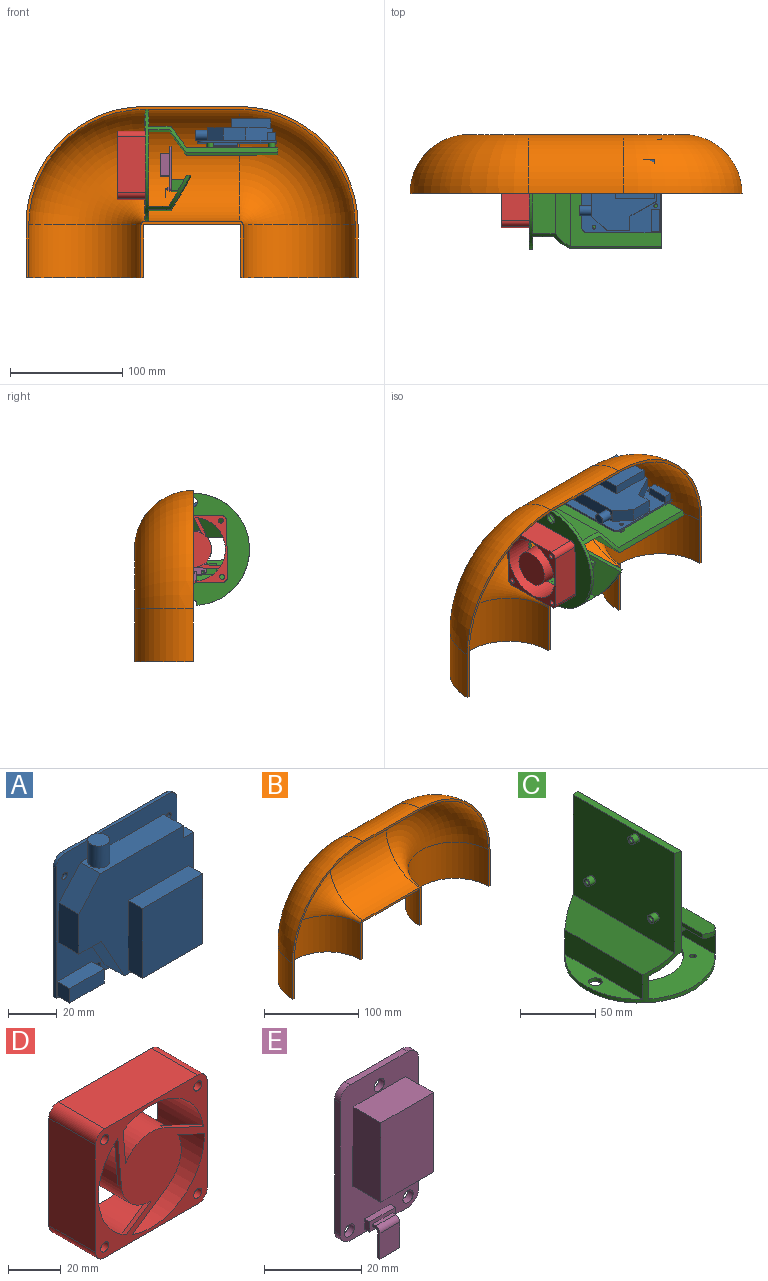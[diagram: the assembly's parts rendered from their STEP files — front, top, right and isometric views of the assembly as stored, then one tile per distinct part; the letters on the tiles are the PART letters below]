
ASSEMBLY  parts=5 mates=4
PART A: 39 faces, bbox 70x24.3x72.1 mm
  f0: plane 65x1.6mm, normal (0,0,-1), area 104mm2, adj f2,f7,f9,f10
  f1: cylinder r=1.6mm len=3.2mm, axis (0,1,0), area 16.1mm2, adj f7,f9
  f2: plane 65x1.6mm, normal (-1,0,0), area 104mm2, adj f0,f7,f9,f37
  f3: plane 60x1.6mm, normal (1,0,0), area 96mm2, adj f4,f7,f9,f10
  f4: cylinder r=5mm len=5mm, axis (0,1,0), area 12.6mm2, adj f3,f7,f9,f38
  f5: cylinder r=1.6mm len=3.2mm, axis (0,1,0), area 16.1mm2, adj f7,f9
  f6: cylinder r=1.6mm len=3.2mm, axis (0,1,0), area 16.1mm2, adj f7,f9
  f7: plane 70x70mm, normal (0,-1,0), area 1459.9mm2, adj f0,f1,f2,f3,f4,f5,f6,f10
  f8: plane 25x3mm, normal (0,0,1), area 75mm2, adj f9,f28,f29,f31
  f9: plane 70x70mm, normal (0,1,0), area 4234.8mm2, adj f0,f1,f2,f3,f4,f5,f6,f8
  f10: cylinder r=5mm len=5mm, axis (0,1,0), area 12.6mm2, adj f0,f3,f7,f9
  f11: plane 14.1x12.5mm, normal (-0.75,0,0.66), area 216.7mm2, adj f7,f12,f24,f27
  f12: plane 20x11.5mm, normal (-1,0,0), area 230mm2, adj f7,f11,f13,f24
  f13: plane 13x11.5mm, normal (0,0,-1), area 149.5mm2, adj f7,f12,f14,f24
  f14: plane 24x13.3mm, normal (-0.87,0,-0.48), area 315.5mm2, adj f7,f13,f15,f24
  f15: plane 40x11.5mm, normal (0,0,-1), area 460mm2, adj f7,f14,f16,f24
  f16: plane 52x11.5mm, normal (1,0,0), area 598mm2, adj f7,f15,f17,f24
  f17: plane 11.5x5.8mm, normal (0,0,1), area 66.7mm2, adj f7,f16,f18,f24
  f18: plane 11.5x6.1mm, normal (1,0,0), area 70.2mm2, adj f7,f17,f24,f27
  f19: plane 35x8.2mm, normal (1,0,0), area 287mm2, adj f20,f22,f23,f24
  f20: plane 35x8.2mm, normal (0,0,1), area 287mm2, adj f19,f21,f23,f24
  f21: plane 35x8.2mm, normal (-1,0,0), area 287mm2, adj f20,f22,f23,f24
  f22: plane 35x8.2mm, normal (0,0,-1), area 287mm2, adj f19,f21,f23,f24
  f23: plane 35x35mm, normal (0,-1,0), area 1225mm2, adj f19,f20,f21,f22
  f24: plane 66.3x58.1mm, normal (0,-1,0), area 2031.9mm2, adj f11,f12,f13,f14,f15,f16,f17,f18
  f25: cylinder r=4.5mm len=11mm, axis (0,0,1), area 311mm2, adj f26,f27
  f26: plane 9x9mm, normal (0,0,1), area 63.6mm2, adj f25
  f27: plane 48x11.5mm, normal (0,0,1), area 488.4mm2, adj f7,f11,f18,f24,f25
  f28: plane 25x25mm, normal (0,1,0), area 625mm2, adj f8,f29,f30,f31
  f29: plane 25x3mm, normal (-1,0,0), area 75mm2, adj f8,f9,f28,f30
  f30: plane 25x3mm, normal (0,0,-1), area 75mm2, adj f9,f28,f29,f31
  f31: plane 25x3mm, normal (1,0,0), area 75mm2, adj f8,f9,f28,f30
  f32: plane 20x7.2mm, normal (0,0,-1), area 144mm2, adj f7,f33,f35,f36
  f33: plane 7.2x7.15mm, normal (1,0,0), area 51.5mm2, adj f7,f32,f34,f36
  f34: plane 20x7.2mm, normal (0,0,1), area 144mm2, adj f7,f33,f35,f36
  f35: plane 7.2x7.15mm, normal (-1,0,0), area 51.5mm2, adj f7,f32,f34,f36
  f36: plane 20x7.15mm, normal (0,-1,0), area 143mm2, adj f32,f33,f34,f35
  f37: cylinder r=5mm len=5mm, axis (0,1,0), area 12.6mm2, adj f2,f7,f9,f38
  f38: plane 60x1.6mm, normal (0,0,1), area 96mm2, adj f4,f7,f9,f37
PART B: 14 faces, bbox 313.4x89.8x161.2 mm
  f0: plane 91x50mm, normal (0,-1,0), area 461.2mm2, adj f1,f2,f3,f4,f5,f6,f7,f8
  f1: cylinder r=52.5mm len=105mm, axis (0,0,-1), area 7751.9mm2, adj f0,f2,f6,f13
  f2: torus R=53mm, axis (0,1,0), area 13731.1mm2, adj f0,f1,f3,f13
  f3: cylinder r=52.5mm len=105mm, axis (1,0,0), area 14019.4mm2, adj f0,f2,f4,f13
  f4: torus R=53mm, axis (0,1,0), area 13731.1mm2, adj f0,f3,f5,f13
  f5: cylinder r=52.5mm len=105mm, axis (0,0,1), area 7751.9mm2, adj f0,f4,f7,f13
  f6: plane 105x52.5mm, normal (0,0,-1), area 402.5mm2, adj f0,f1,f8,f13
  f7: plane 105x52.5mm, normal (0,0,-1), area 402.5mm2, adj f0,f5,f12,f13
  f8: cylinder r=50mm len=100mm, axis (0,0,-1), area 7382.7mm2, adj f0,f6,f9,f13
  f9: torus R=53mm, axis (0,1,0), area 13077.2mm2, adj f0,f8,f10,f13
  f10: cylinder r=50mm len=100mm, axis (1,0,0), area 13351.8mm2, adj f0,f9,f11,f13
  f11: torus R=53mm, axis (0,1,0), area 13077.2mm2, adj f0,f10,f12,f13
  f12: cylinder r=50mm len=100mm, axis (0,0,1), area 7382.7mm2, adj f0,f7,f11,f13
  f13: plane 296x152.5mm, normal (0,-1,0), area 1266.3mm2, adj f1,f2,f3,f4,f5,f6,f7,f8
PART C: 47 faces, bbox 100x100x118 mm
  f0: plane 100x68mm, normal (0,0,1), area 3514.8mm2, adj f2,f5,f7,f8,f9,f11,f16,f22
  f1: plane 60x9.96mm, normal (0,0,1), area 394.5mm2, adj f2,f3,f4,f10,f17
  f2: cylinder r=50mm len=118mm, axis (0,0,1), area 2506.6mm2, adj f0,f1,f3,f10,f12,f13,f14,f15
  f3: plane 3x1.96mm, normal (0,1,0), area 5.9mm2, adj f1,f2,f4,f12
  f4: cylinder r=2mm len=4mm, axis (0,0,1), area 18.8mm2, adj f1,f3,f10,f12
  f5: cylinder r=2.15mm len=4.3mm, axis (0,0,1), area 40.5mm2, adj f0,f12
  f6: cylinder r=4.5mm len=9mm, axis (0,0,1), area 84.8mm2, adj f12,f13
  f7: cylinder r=2.15mm len=4.3mm, axis (0,0,1), area 40.5mm2, adj f0,f12
  f8: cylinder r=2.15mm len=4.3mm, axis (0,0,1), area 40.5mm2, adj f0,f12
  f9: cylinder r=29mm len=58mm, axis (0,0,1), area 546.6mm2, adj f0,f12
  f10: plane 3x1.96mm, normal (0,-1,0), area 5.9mm2, adj f1,f2,f4,f12
  f11: cylinder r=2.15mm len=4.3mm, axis (0,0,1), area 40.5mm2, adj f0,f12
  f12: plane 100x99.96mm, normal (0,0,-1), area 5076mm2, adj f2,f3,f4,f5,f6,f7,f8,f9
  f13: plane 73.32x16mm, normal (0,0,1), area 747.5mm2, adj f2,f6,f24
  f14: plane 97.98x30mm, normal (0.5,0,0.87), area 2915.6mm2, adj f2,f17,f18
  f15: plane 97.98x27mm, normal (-0.5,0,-0.87), area 2232.9mm2, adj f2,f16,f18,f26,f27,f29,f30
  f16: plane 67.26x18.27mm, normal (-1,0,0), area 1228.7mm2, adj f0,f2,f15
  f17: plane 60x20mm, normal (1,0,0), area 1200mm2, adj f1,f2,f14
  f18: plane 97.98x3.46mm, normal (-1,0,0), area 339.4mm2, adj f2,f14,f15
  f19: plane 97.98x5mm, normal (0,0,1), area 483.9mm2, adj f2,f21,f25
  f20: plane 97.98x21mm, normal (0.59,0,-0.81), area 2336.6mm2, adj f2,f21,f22
  f21: plane 97.98x81.38mm, normal (1,0,0), area 7973.5mm2, adj f2,f19,f20
  f22: plane 78.46x18.47mm, normal (1,0,0), area 1448.8mm2, adj f0,f2,f20
  f23: plane 95.39x19mm, normal (-0.59,0,0.81), area 2020.9mm2, adj f2,f24,f25
  f24: plane 73.32x20mm, normal (-1,0,0), area 1466.4mm2, adj f2,f13,f23
  f25: plane 95.39x81.29mm, normal (-1,0,0), area 7669.6mm2, adj f2,f19,f23,f36,f40,f44
  f26: plane 40x6.35mm, normal (1,0,0), area 254mm2, adj f15,f28,f29,f30
  f27: plane 40x12.12mm, normal (-1,0,0), area 485mm2, adj f15,f28,f29,f30
  f28: plane 40x10mm, normal (0,0,-1), area 388.5mm2, adj f26,f27,f29,f30,f31,f33
  f29: plane 12.12x10mm, normal (0,1,0), area 92.4mm2, adj f15,f26,f27,f28
  f30: plane 12.12x10mm, normal (0,-1,0), area 92.4mm2, adj f15,f26,f27,f28
  f31: cylinder r=1.35mm len=7mm, axis (0,0,-1), area 59.4mm2, adj f28,f32
  f32: cone r=0mm half-angle=59deg, axis (0,0,-1), area 6.7mm2, adj f31
  f33: cylinder r=1.35mm len=7mm, axis (0,0,-1), area 59.4mm2, adj f28,f34
  f34: cone r=0mm half-angle=59deg, axis (0,0,-1), area 6.7mm2, adj f33
  f35: cylinder r=1.6mm len=5mm, axis (1,0,0), area 50.3mm2, adj f37,f38
  f36: cylinder r=3mm len=6mm, axis (1,0,0), area 94.2mm2, adj f25,f37
  f37: plane 6x6mm, normal (-1,0,0), area 20.2mm2, adj f35,f36
  f38: plane 3.2x3.2mm, normal (-1,0,0), area 8mm2, adj f35
  f39: cylinder r=1.6mm len=5mm, axis (1,0,0), area 50.3mm2, adj f41,f42
  f40: cylinder r=3mm len=6mm, axis (1,0,0), area 94.2mm2, adj f25,f41
  f41: plane 6x6mm, normal (-1,0,0), area 20.2mm2, adj f39,f40
  f42: plane 3.2x3.2mm, normal (-1,0,0), area 8mm2, adj f39
  f43: cylinder r=1.6mm len=5mm, axis (1,0,0), area 50.3mm2, adj f45,f46
  f44: cylinder r=3mm len=6mm, axis (1,0,0), area 94.2mm2, adj f25,f45
  f45: plane 6x6mm, normal (-1,0,0), area 20.2mm2, adj f43,f44
  f46: plane 3.2x3.2mm, normal (-1,0,0), area 8mm2, adj f43
PART D: 26 faces, bbox 60x25x60 mm
  f0: plane 21.59x13.54mm, normal (0,1,0), area 54.3mm2, adj f2,f18,f21,f22
  f1: plane 25.47x4.14mm, normal (0,1,0), area 54.3mm2, adj f2,f17,f18,f23
  f2: cylinder r=28.5mm len=57mm, axis (0,-1,0), area 4455.8mm2, adj f0,f1,f15,f16,f17,f19,f20,f21
  f3: plane 50x25mm, normal (0,0,1), area 1250mm2, adj f4,f13,f15,f16
  f4: cylinder r=5mm len=25mm, axis (0,-1,0), area 196.3mm2, adj f3,f5,f15,f16
  f5: plane 50x25mm, normal (-1,0,0), area 1250mm2, adj f4,f6,f15,f16
  f6: cylinder r=5mm len=25mm, axis (0,-1,0), area 196.3mm2, adj f5,f7,f15,f16
  f7: plane 50x25mm, normal (0,0,-1), area 1250mm2, adj f6,f8,f15,f16
  f8: cylinder r=5mm len=25mm, axis (0,-1,0), area 196.3mm2, adj f7,f9,f15,f16
  f9: plane 50x25mm, normal (1,0,0), area 1250mm2, adj f8,f13,f15,f16
  f10: cylinder r=2.15mm len=25mm, axis (0,-1,0), area 337.7mm2, adj f15,f16
  f11: cylinder r=2.15mm len=25mm, axis (0,-1,0), area 337.7mm2, adj f15,f16
  f12: cylinder r=2.15mm len=25mm, axis (0,-1,0), area 337.7mm2, adj f15,f16
  f13: cylinder r=5mm len=25mm, axis (0,-1,0), area 196.3mm2, adj f3,f9,f15,f16
  f14: cylinder r=2.15mm len=25mm, axis (0,-1,0), area 337.7mm2, adj f15,f16
  f15: plane 60x60mm, normal (0,1,0), area 968.7mm2, adj f2,f3,f4,f5,f6,f7,f8,f9
  f16: plane 60x60mm, normal (0,-1,0), area 1945.8mm2, adj f2,f3,f4,f5,f6,f7,f8,f9
  f17: plane 23.44x2mm, normal (-1,0,-0.08), area 47mm2, adj f1,f2,f16,f18
  f18: cylinder r=16.1mm len=32.2mm, axis (0,-1,0), area 2469.1mm2, adj f0,f1,f16,f17,f19,f20,f21,f22
  f19: plane 13.12x9.07mm, normal (-0.57,0,0.82), area 31.9mm2, adj f2,f16,f18,f24
  f20: plane 19.34x13.38mm, normal (0.57,0,-0.82), area 47mm2, adj f2,f16,f18,f24
  f21: plane 14.42x6.83mm, normal (-0.43,0,-0.9), area 31.9mm2, adj f0,f2,f16,f18
  f22: plane 21.25x10.06mm, normal (0.43,0,0.9), area 47mm2, adj f0,f2,f16,f18
  f23: plane 15.9x2mm, normal (1,0,0.08), area 31.9mm2, adj f1,f2,f16,f18
  f24: plane 22.53x13.38mm, normal (0,1,0), area 54.3mm2, adj f2,f18,f19,f20
  f25: plane 32.2x32.2mm, normal (0,1,0), area 814.3mm2, adj f18
PART E: 32 faces, bbox 22.8x9.7x44.6 mm
  f0: plane 39.2x22.8mm, normal (0,-1,0), area 540.1mm2, adj f1,f2,f3,f4,f5,f6,f7,f8
  f1: plane 33.2x1.6mm, normal (1,0,0), area 53.1mm2, adj f0,f2,f11,f12
  f2: cylinder r=3mm len=3mm, axis (0,-1,0), area 7.5mm2, adj f0,f1,f3,f12
  f3: plane 16.8x1.6mm, normal (0,0,1), area 26.9mm2, adj f0,f2,f4,f12
  f4: cylinder r=3mm len=3mm, axis (0,-1,0), area 7.5mm2, adj f0,f3,f5,f12
  f5: plane 33.2x1.6mm, normal (-1,0,0), area 53.1mm2, adj f0,f4,f6,f12
  f6: cylinder r=3mm len=3mm, axis (0,-1,0), area 7.5mm2, adj f0,f5,f7,f12
  f7: plane 16.8x1.6mm, normal (0,0,-1), area 26.9mm2, adj f0,f6,f11,f12
  f8: cylinder r=1.5mm len=3mm, axis (0,-1,0), area 15.1mm2, adj f0,f12
  f9: cylinder r=1.5mm len=3mm, axis (0,-1,0), area 15.1mm2, adj f0,f12
  f10: cylinder r=1.5mm len=3mm, axis (0,-1,0), area 15.1mm2, adj f0,f12
  f11: cylinder r=3mm len=3mm, axis (0,-1,0), area 7.5mm2, adj f0,f1,f7,f12
  f12: plane 39.2x22.8mm, normal (0,1,0), area 864.8mm2, adj f1,f2,f3,f4,f5,f6,f7,f8
  f13: plane 15.3x8.12mm, normal (0,0,1), area 124.2mm2, adj f0,f14,f16,f17
  f14: plane 20x8.12mm, normal (-1,0,0), area 162.4mm2, adj f0,f13,f15,f17
  f15: plane 15.3x8.12mm, normal (0,0,-1), area 124.2mm2, adj f0,f14,f16,f17
  f16: plane 20x8.12mm, normal (1,0,0), area 162.4mm2, adj f0,f13,f15,f17
  f17: plane 20x15.3mm, normal (0,-1,0), area 306mm2, adj f13,f14,f15,f16
  f18: plane 7.38x1.5mm, normal (0,0,1), area 11.1mm2, adj f0,f19,f21,f22
  f19: plane 2.54x1.5mm, normal (-1,0,0), area 3.8mm2, adj f0,f18,f20,f22
  f20: plane 7.38x1.5mm, normal (0,0,-1), area 11.1mm2, adj f0,f19,f21,f22
  f21: plane 2.54x1.5mm, normal (1,0,0), area 3.8mm2, adj f0,f18,f20,f22
  f22: plane 7.38x2.54mm, normal (0,-1,0), area 15.1mm2, adj f18,f19,f20,f21,f28,f29,f30,f31
  f23: cylinder r=0.6mm len=5.73mm, axis (1,0,0), area 5.4mm2, adj f24,f28,f29,f30
  f24: plane 6.5x5.73mm, normal (0,1,0), area 37.2mm2, adj f23,f25,f28,f30
  f25: plane 5.73x0.63mm, normal (0,0,-1), area 3.6mm2, adj f24,f26,f28,f30
  f26: plane 6.5x5.73mm, normal (0,-1,0), area 37.2mm2, adj f25,f27,f28,f30
  f27: cylinder r=1.23mm len=5.73mm, axis (1,0,0), area 11.1mm2, adj f26,f28,f30,f31
  f28: plane 7.73x2.13mm, normal (1,0,0), area 5.6mm2, adj f22,f23,f24,f25,f26,f27,f29,f31
  f29: plane 5.73x0.9mm, normal (0,0,-1), area 5.2mm2, adj f22,f23,f28,f30
  f30: plane 7.73x2.13mm, normal (-1,0,0), area 5.6mm2, adj f22,f23,f24,f25,f26,f27,f29,f31
  f31: plane 5.73x0.9mm, normal (0,0,1), area 5.2mm2, adj f22,f27,f28,f30
PLACE A rot(axis=(-0.58,-0.57,0.58),120.7deg) t=(39.49,26.91,108.57)mm
PLACE B t=(41.92,27.15,86.96)mm fixed
PLACE C rot(axis=(-0.01,1,-0.01),90deg) t=(-39.22,27.15,86.96)mm
PLACE D rot(axis=(0.57,-0.57,0.59),119.3deg) t=(-42.22,27.15,86.96)mm
PLACE E rot(axis=(-0.01,-0.01,-1),90deg) t=(-20.82,27.56,87.39)mm
MATE fastened A.f6 <-> C.f43  axis (0,-0.02,-1) through (70.49,16.07,107.2)mm
MATE fastened D.f4 <-> C.f8  axis (1,0,0) through (-42.22,1.63,62.49)mm
MATE fastened E.f10 <-> C.f33  axis (1,0,0) through (-19.22,18.72,66.93)mm
MATE cylindrical B.f10 <-> C.f2  axis (1,0,0) through (-43.08,27.15,86.96)mm
